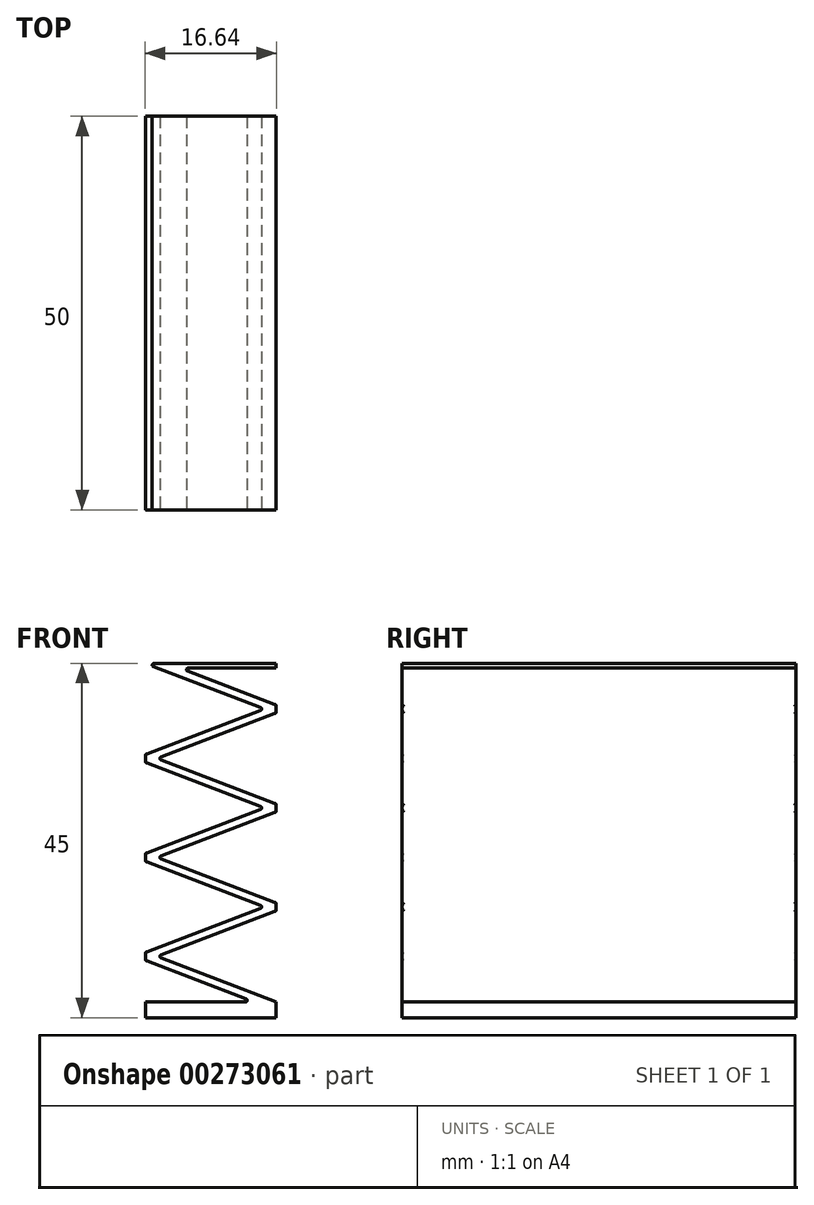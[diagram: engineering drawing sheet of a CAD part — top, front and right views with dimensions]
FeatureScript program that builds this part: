
annotation { "Feature Type Name" : "Feature", "Feature Type Description" : "" }
export const myFeature = defineFeature(function(context is Context, id is Id, definition is map)
    precondition{}
    {
        {
            var Q0;
            Q0=qCreatedBy(makeId("Front.planeOp"),FACE);
            var sketch = newSketch(context, id + "F0", { "sketchPlane" : qUnion([Q0])});
            skLineSegment(sketch, "E0", {"start": v(-8.32, 0) * mm, "end": v(-8.32, 2) * mm});
            skLineSegment(sketch, "E1", {"start": v(-8.32, 2) * mm, "end": v(8.32, 2) * mm});
            skLineSegment(sketch, "E2", {"start": v(8.32, 2) * mm, "end": v(8.32, 0) * mm});
            skLineSegment(sketch, "E3", {"start": v(8.32, 0) * mm, "end": v(-8.32, 0) * mm});
            skLineSegment(sketch, "E4", {"start": v(-8.32, 7.29) * mm, "end": v(-8.32, 8.29) * mm});
            skLineSegment(sketch, "E5", {"start": v(-8.32, 8.29) * mm, "end": v(6.82, 14.07) * mm});
            skLineSegment(sketch, "E6", {"start": v(6.82, 14.07) * mm, "end": v(-8.32, 19.86) * mm});
            skLineSegment(sketch, "E7", {"start": v(-8.32, 19.86) * mm, "end": v(-8.32, 20.86) * mm});
            skLineSegment(sketch, "E8", {"start": v(-8.32, 20.86) * mm, "end": v(6.82, 26.64) * mm});
            skLineSegment(sketch, "E9", {"start": v(6.82, 26.64) * mm, "end": v(-8.32, 32.43) * mm});
            skLineSegment(sketch, "E10", {"start": v(-8.32, 32.43) * mm, "end": v(-8.32, 33.43) * mm});
            skLineSegment(sketch, "E11", {"start": v(-8.32, 33.43) * mm, "end": v(6.82, 39.21) * mm});
            skLineSegment(sketch, "E12", {"start": v(6.82, 39.21) * mm, "end": v(-8.32, 45) * mm});
            skLineSegment(sketch, "E13", {"start": v(-8.32, 45) * mm, "end": v(8.32, 45) * mm});
            skLineSegment(sketch, "E14", {"start": v(8.32, 39.71) * mm, "end": v(8.32, 38.71) * mm});
            skLineSegment(sketch, "E15", {"start": v(8.32, 38.71) * mm, "end": v(-6.82, 32.93) * mm});
            skLineSegment(sketch, "E16", {"start": v(-6.82, 32.93) * mm, "end": v(8.32, 27.14) * mm});
            skLineSegment(sketch, "E17", {"start": v(8.32, 27.14) * mm, "end": v(8.32, 26.14) * mm});
            skLineSegment(sketch, "E18", {"start": v(8.32, 26.14) * mm, "end": v(-6.82, 20.36) * mm});
            skLineSegment(sketch, "E19", {"start": v(-6.82, 20.36) * mm, "end": v(8.32, 14.57) * mm});
            skLineSegment(sketch, "E20", {"start": v(8.32, 14.57) * mm, "end": v(8.32, 13.57) * mm});
            skLineSegment(sketch, "E21", {"start": v(8.32, 13.57) * mm, "end": v(-6.82, 7.79) * mm});
            skLineSegment(sketch, "E22", {"start": v(-6.82, 7.79) * mm, "end": v(8.32, 2) * mm});
            skLineSegment(sketch, "E23", {"start": v(5.52, 2) * mm, "end": v(-8.32, 7.29) * mm});
            skPoint(sketch, "E24", {"position": v(8.32, 39.21) * mm});
            skPoint(sketch, "E25", {"position": v(-8.32, 32.93) * mm});
            skPoint(sketch, "E26", {"position": v(8.32, 26.64) * mm});
            skPoint(sketch, "E27", {"position": v(-8.32, 20.36) * mm});
            skPoint(sketch, "E28", {"position": v(8.32, 14.07) * mm});
            skPoint(sketch, "E29", {"position": v(-8.32, 7.79) * mm});
            skPoint(sketch, "E30", {"position": v(0, 0) * mm});
            skLineSegment(sketch, "E31", {"start": v(8.32, 45) * mm, "end": v(8.32, 44.41) * mm});
            skLineSegment(sketch, "E32", {"start": v(8.32, 44.41) * mm, "end": v(-3.97, 44.41) * mm});
            skLineSegment(sketch, "E33", {"start": v(-3.97, 44.41) * mm, "end": v(8.32, 39.71) * mm});
            skSolve(sketch);
        }
        {
            var Q0;
            Q0 = qSketchRegion(id + "F0", true);
            extrude(context, id + "F1", {"entities" : qUnion([Q0]), "endBound" : BoundingType.SYMMETRIC, "depth" : 50 * mm});
        }
        {
            var Q0;
            Q0=makeQuery(id+"F1.opExtrude","SWEPT_EDGE",EDGE,{"disambiguationData":[OSD([sQuery(id+"F0.wireOp",EDGE,"E15"),sQuery(id+"F0.wireOp",EDGE,"E16")])]});
            var Q1;
            Q1=makeQuery(id+"F1.opExtrude","SWEPT_EDGE",EDGE,{"disambiguationData":[OSD([sQuery(id+"F0.wireOp",EDGE,"E32"),sQuery(id+"F0.wireOp",EDGE,"E33")])]});
            var Q2;
            Q2=makeQuery(id+"F1.opExtrude","SWEPT_EDGE",EDGE,{"disambiguationData":[OSD([sQuery(id+"F0.wireOp",EDGE,"E18"),sQuery(id+"F0.wireOp",EDGE,"E19")])]});
            var Q3;
            Q3=makeQuery(id+"F1.opExtrude","SWEPT_EDGE",EDGE,{"disambiguationData":[OSD([sQuery(id+"F0.wireOp",EDGE,"E21"),sQuery(id+"F0.wireOp",EDGE,"E22")])]});
            var Q4;
            Q4=makeQuery(id+"F1.opExtrude","SWEPT_EDGE",EDGE,{"disambiguationData":[OSD([sQuery(id+"F0.wireOp",EDGE,"E1"),sQuery(id+"F0.wireOp",EDGE,"E23")])]});
            var Q5;
            Q5=makeQuery(id+"F1.opExtrude","SWEPT_EDGE",EDGE,{"disambiguationData":[OSD([sQuery(id+"F0.wireOp",EDGE,"E5"),sQuery(id+"F0.wireOp",EDGE,"E6")])]});
            var Q6;
            Q6=makeQuery(id+"F1.opExtrude","SWEPT_EDGE",EDGE,{"disambiguationData":[OSD([sQuery(id+"F0.wireOp",EDGE,"E8"),sQuery(id+"F0.wireOp",EDGE,"E9")])]});
            var Q7;
            Q7=makeQuery(id+"F1.opExtrude","SWEPT_EDGE",EDGE,{"disambiguationData":[OSD([sQuery(id+"F0.wireOp",EDGE,"E11"),sQuery(id+"F0.wireOp",EDGE,"E12")])]});
            fillet(context, id + "F2", {"entities" : qUnion([Q0, Q1, Q2, Q3, Q4, Q5, Q6, Q7]), "radius" : 0.2 * mm, "tangentPropagation" : true, "allowEdgeOverflow" : false});
        }
        {
            var Q0;
            Q0=makeQuery(id+"F1.opExtrude","SWEPT_FACE",FACE,{"disambiguationData":[OSD([sQuery(id+"F0.wireOp",EDGE,"E4")])]});
            var Q1;
            Q1=makeQuery(id+"F1.opExtrude","SWEPT_FACE",FACE,{"disambiguationData":[OSD([sQuery(id+"F0.wireOp",EDGE,"E7")])]});
            var Q2;
            Q2=makeQuery(id+"F1.opExtrude","SWEPT_FACE",FACE,{"disambiguationData":[OSD([sQuery(id+"F0.wireOp",EDGE,"E10")])]});
            var Q3;
            Q3=makeQuery(id+"F1.opExtrude","SWEPT_EDGE",EDGE,{"disambiguationData":[OSD([sQuery(id+"F0.wireOp",EDGE,"E12"),sQuery(id+"F0.wireOp",EDGE,"E13")])]});
            var Q4;
            Q4=makeQuery(id+"F1.opExtrude","SWEPT_FACE",FACE,{"disambiguationData":[OSD([sQuery(id+"F0.wireOp",EDGE,"E14")])]});
            var Q5;
            Q5=makeQuery(id+"F1.opExtrude","SWEPT_FACE",FACE,{"disambiguationData":[OSD([sQuery(id+"F0.wireOp",EDGE,"E17")])]});
            var Q6;
            Q6=makeQuery(id+"F1.opExtrude","SWEPT_FACE",FACE,{"disambiguationData":[OSD([sQuery(id+"F0.wireOp",EDGE,"E20")])]});
            fillet(context, id + "F3", {"entities" : qUnion([Q0, Q1, Q2, Q3, Q4, Q5, Q6]), "radius" : 0.2 * mm, "tangentPropagation" : true, "allowEdgeOverflow" : false});
        }
    });
